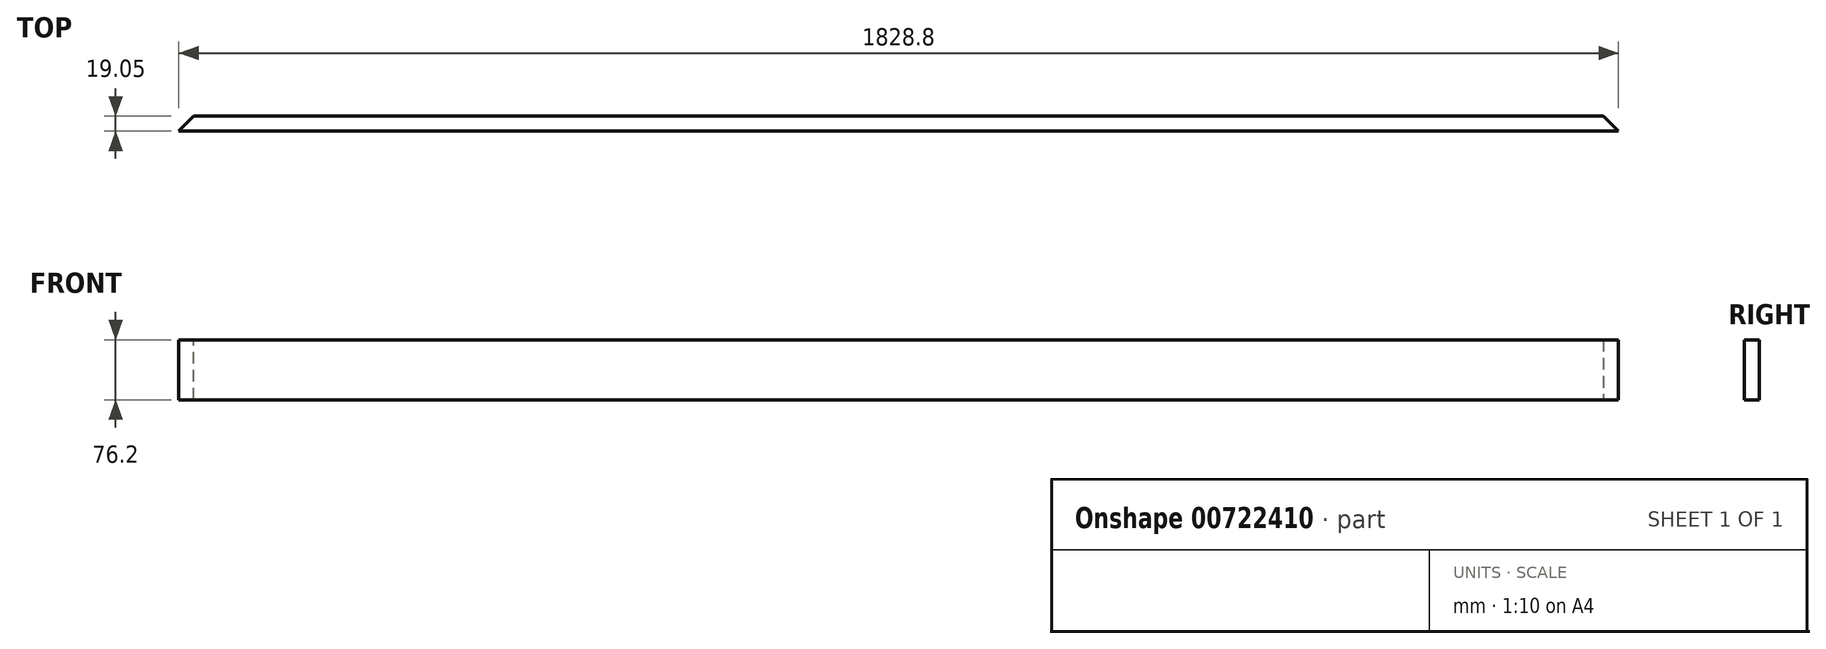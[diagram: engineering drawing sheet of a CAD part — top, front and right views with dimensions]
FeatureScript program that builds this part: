
annotation { "Feature Type Name" : "Feature", "Feature Type Description" : "" }
export const myFeature = defineFeature(function(context is Context, id is Id, definition is map)
    precondition{}
    {
        {
            var Q0;
            Q0=qCreatedBy(makeId("Front.planeOp"),FACE);
            var sketch = newSketch(context, id + "F0", { "sketchPlane" : qUnion([Q0])});
            skLineSegment(sketch, "E0.bottom", {"start": v(914.4, -38.1) * mm, "end": v(-914.4, -38.1) * mm});
            skLineSegment(sketch, "E0.top", {"start": v(914.4, 38.1) * mm, "end": v(-914.4, 38.1) * mm});
            skLineSegment(sketch, "E0.left", {"start": v(914.4, -38.1) * mm, "end": v(914.4, 38.1) * mm});
            skLineSegment(sketch, "E0.right", {"start": v(-914.4, -38.1) * mm, "end": v(-914.4, 38.1) * mm});
            skPoint(sketch, "E0.middle", {"position": v(0, 0) * mm});
            skSolve(sketch);
        }
        {
            var Q0;
            Q0=makeQuery(id+"F0.imprint","IMPRINT",FACE,{"disambiguationData":[TD([[makeQuery(id+"F0.imprint","IMPRINT",EDGE,{"derivedFrom":sQuery(id+"F0.wireOp",EDGE,"E0.bottom")}),-1.0]])]});
            extrude(context, id + "F1", {"entities" : qUnion([Q0]), "depth" : 19.05 * mm, "offsetDistance" : 25.4 * mm});
        }
        {
            var Q0;
            Q0=makeQuery(id+"F1.opExtrude","CAP_EDGE",EDGE,{"disambiguationData":[OSD([sQuery(id+"F0.wireOp",EDGE,"E0.right")])],"isStart":true});
            var Q1;
            Q1=makeQuery(id+"F1.opExtrude","CAP_EDGE",EDGE,{"disambiguationData":[OSD([sQuery(id+"F0.wireOp",EDGE,"E0.left")])],"isStart":true});
            chamfer(context, id + "F2", {"entities" : qUnion([Q0, Q1]), "width" : 19.05 * mm, "tangentPropagation" : true});
        }
    });
